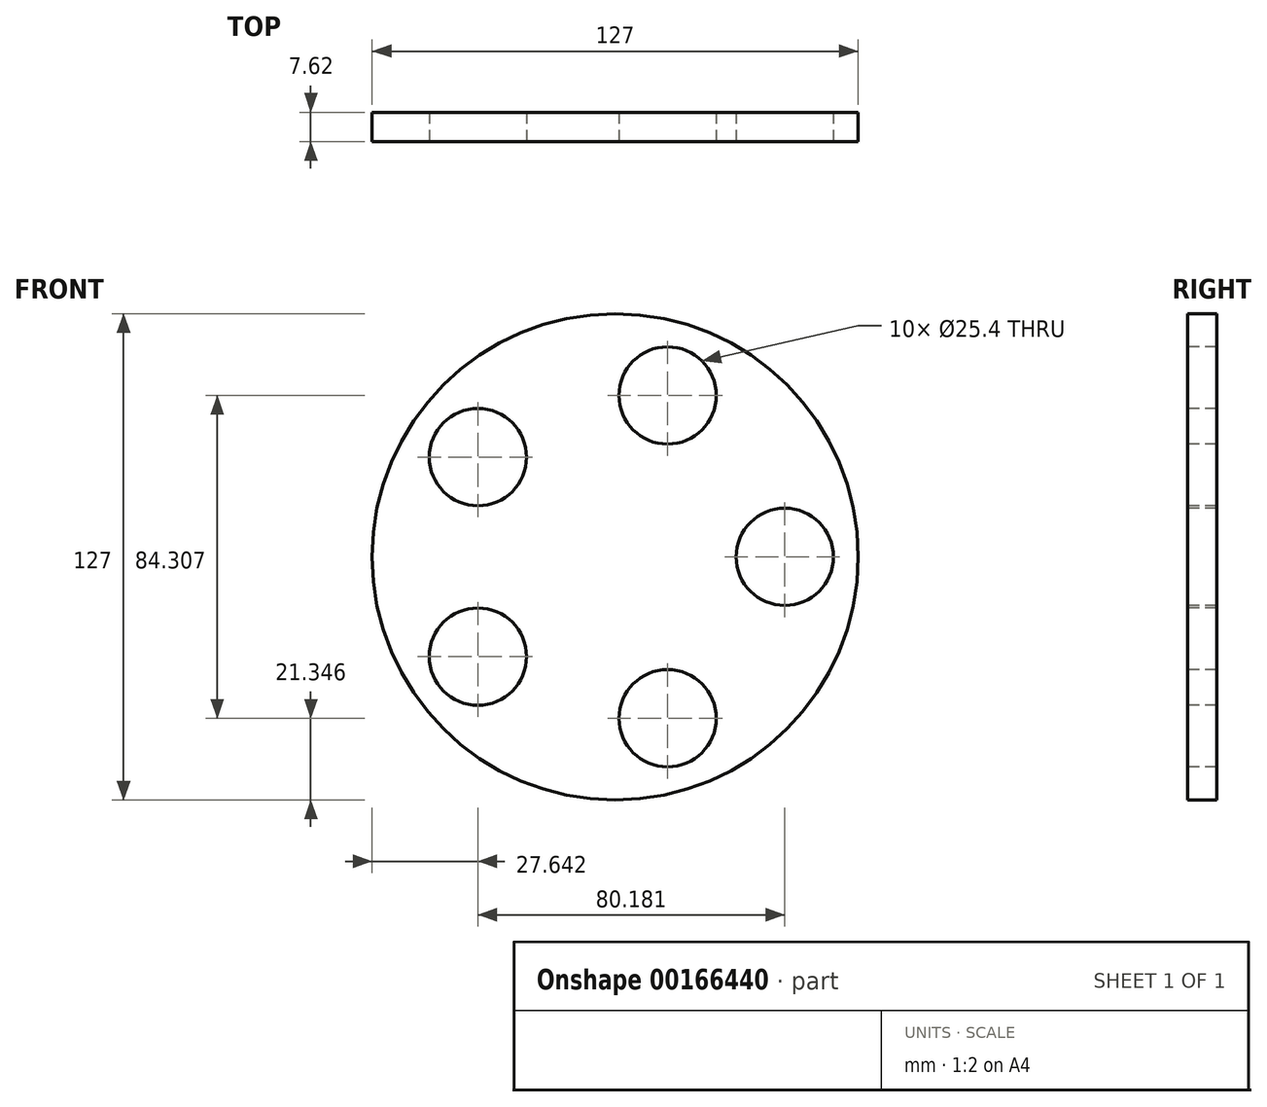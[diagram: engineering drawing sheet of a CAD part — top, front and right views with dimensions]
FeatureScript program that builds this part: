
annotation { "Feature Type Name" : "Feature", "Feature Type Description" : "" }
export const myFeature = defineFeature(function(context is Context, id is Id, definition is map)
    precondition{}
    {
        {
            var Q0;
            Q0=qCreatedBy(makeId("Front.planeOp"),FACE);
            var sketch = newSketch(context, id + "F0", { "sketchPlane" : qUnion([Q0])});
            skCircle(sketch, "E0", {"center": v(0, 0) * mm, "radius": 63.5 * mm});
            skSolve(sketch);
        }
        {
            var Q0;
            Q0=makeQuery(id+"F0.imprint","IMPRINT",FACE,{"disambiguationData":[TD([[makeQuery(id+"F0.imprint","IMPRINT",EDGE,{"derivedFrom":sQuery(id+"F0.wireOp",EDGE,"E0")}),1.0]])]});
            extrude(context, id + "F1", {"entities" : qUnion([Q0]), "endBound" : BoundingType.SYMMETRIC, "depth" : 7.62 * mm});
        }
        {
            var Q0;
            Q0=makeQuery(id+"F1.opExtrude","CAP_FACE",FACE,{"disambiguationData":[OSD([sQuery(id+"F0.wireOp",EDGE,"E0")])],"isStart":false});
            var sketch = newSketch(context, id + "F2", { "sketchPlane" : qUnion([Q0])});
            skCircle(sketch, "E1", {"center": v(44.32, 0) * mm, "radius": 12.7 * mm});
            skCircle(sketch, "E2.1.0", {"center": v(13.7, 42.15) * mm, "radius": 12.7 * mm});
            skCircle(sketch, "E2.2.0", {"center": v(-35.86, 26.05) * mm, "radius": 12.7 * mm});
            skCircle(sketch, "E2.3.0", {"center": v(-35.86, -26.05) * mm, "radius": 12.7 * mm});
            skCircle(sketch, "E2.4.0", {"center": v(13.7, -42.15) * mm, "radius": 12.7 * mm});
            skPoint(sketch, "E2.center", {"position": v(0, 0) * mm});
            skSolve(sketch);
        }
        {
            var Q0;
            Q0=makeQuery(id+"F2.imprint","IMPRINT",FACE,{"disambiguationData":[TD([[makeQuery(id+"F2.imprint","IMPRINT",EDGE,{"derivedFrom":sQuery(id+"F2.wireOp",EDGE,"E2.2.0")}),1.0]])]});
            var Q1;
            Q1=makeQuery(id+"F2.imprint","IMPRINT",FACE,{"disambiguationData":[TD([[makeQuery(id+"F2.imprint","IMPRINT",EDGE,{"derivedFrom":sQuery(id+"F2.wireOp",EDGE,"E2.1.0")}),1.0]])]});
            var Q2;
            Q2=makeQuery(id+"F2.imprint","IMPRINT",FACE,{"disambiguationData":[TD([[makeQuery(id+"F2.imprint","IMPRINT",EDGE,{"derivedFrom":sQuery(id+"F2.wireOp",EDGE,"E1")}),1.0]])]});
            var Q3;
            Q3=makeQuery(id+"F2.imprint","IMPRINT",FACE,{"disambiguationData":[TD([[makeQuery(id+"F2.imprint","IMPRINT",EDGE,{"derivedFrom":sQuery(id+"F2.wireOp",EDGE,"E2.4.0")}),1.0]])]});
            var Q4;
            Q4=makeQuery(id+"F2.imprint","IMPRINT",FACE,{"disambiguationData":[TD([[makeQuery(id+"F2.imprint","IMPRINT",EDGE,{"derivedFrom":sQuery(id+"F2.wireOp",EDGE,"E2.3.0")}),1.0]])]});
            extrude(context, id + "F3", {"entities" : qUnion([Q0, Q1, Q2, Q3, Q4]), "operationType" : NewBodyOperationType.REMOVE, "endBound" : BoundingType.THROUGH_ALL, "oppositeDirection" : true, "depth" : 7.62 * mm});
        }
    });
